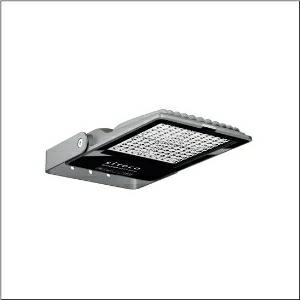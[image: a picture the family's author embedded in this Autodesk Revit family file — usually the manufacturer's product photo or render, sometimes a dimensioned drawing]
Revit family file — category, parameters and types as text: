
# Revit family: sicompact_r__31_mini___pl32_5xa7571f2k23_7a3f
name_source: partatom
category: Lighting Fixtures
units: mm (PartAtom-declared; Revit-internal decimal feet)

## family parameters
Cut with Voids When Loaded = No
Host = Face
Light Source = No
Part Type = Normal
Room Calculation Point = No
Round Connector Dimension = Use Diameter
Shared = No

## types (1)
- SiCompact® 31 mini  PL32 (1 x LED, 20000 lm, 130 W, 4000K)
    Apparent Load = 130 VA
    CIE Flux Codes = 32 69 98 100 100
    Color Rendering = 70
    Color Temperature = 4000K
    Default Elevation = 1800 mm
    Description = SiCompact® 31 mini, floodlight, primary light control with lens, of plastic, of toughened safety glass, transparent, light distribution: PL32, light emission: direct distribution, primary light characteristic: asymmetric, installation type: surface-mounted, LED, High Power LED, rated luminous flux: 20.000lm, luminous efficacy: 154lm/W, light colour: 740, colour temperature: 4000K, control gear: ON/OFF, with cable, 3x 1.5mm², mains connection: 220..240V, AC, 50/60Hz, connection cable pre-assembled, cable length: 2m, rated input power: 130W, of diecast aluminium, specular, metallic grey (RAL 9006), length: 461mm, width: 261mm, height: 62mm, bracket, of sheet steel, coated, metallic grey (RAL 9006), ON/OFF, protection rating (complete): IP66, insulation class (complete): insulation class I (protective earthing), certification: CE, ENEC, impact resistance: IK08, permissible operating ambient temperature: -40..+45°C, packaging unit: 1 piece

Light Distribution: PL32
    Height = 62 mm  [stored 0.203412 ft]
    Lamp = 1 x LED
    Lamp Light Flux = 20000 lm
    Lamp Power = 130 W
    Lamp count = 1
    Length = 460 mm
    Luminous efficacy = 154 lm/W
    Manufacturer = Siteco
    ModVariant = No
    Model = 5XA7571F2K23
    Mounting Place = Wall
    Mounting Type = Surface mounted
    Number of Poles = 1
    OnlyDefault = Yes
    Power Factor = 1
    Product Name = SiCompact® 31 mini | PL32
    Product group = floodlight | wall mounted
    ProductGroupID = 2001
    Protection Class = Protection class I
    Protection Degree = IP 66
    RLX_Detail_Level = 1
    RLX_Emergency_Light_Flux = 0 lm
    RLX_Emergency_Type = 0
    RLX_Emergency_Type_DB = No
    RlxData = <blob elided: 127041 chars, md5=d7bc5232>
    Socket = socket
    Standby Power = 0 W
    System Light Flux = 20000 lm
    System Power = 130 W
    Type Comments = Product without accessories
    Type Image = l_1006951.jpg
    URL = http://relux.com
    VarID = ---
    Voltage = 0 V
    Weight = 0.00 kg
    Width = 260 mm

note: [stored X ft] marks values corroborated as IEEE doubles in the binary element streams (Revit-internal decimal feet)

## geometry (parser evidence)
native form markers: Blend x4, Sweep x13
no freeform markers — native parametric forms only
